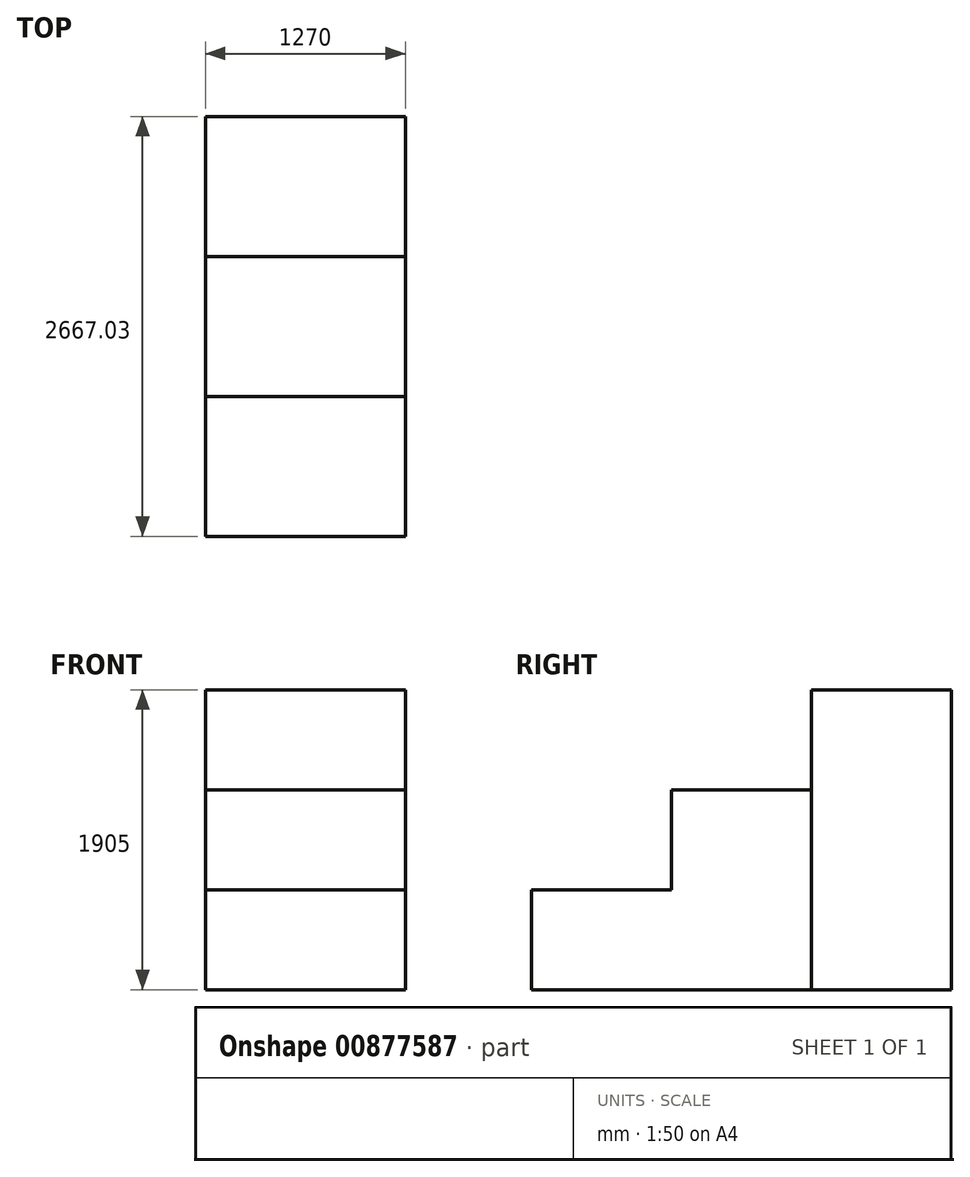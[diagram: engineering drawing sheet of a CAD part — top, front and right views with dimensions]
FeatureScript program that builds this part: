
annotation { "Feature Type Name" : "Feature", "Feature Type Description" : "" }
export const myFeature = defineFeature(function(context is Context, id is Id, definition is map)
    precondition{}
    {
        {
            var Q0;
            Q0=qCreatedBy(makeId("Top.planeOp"),FACE);
            var sketch = newSketch(context, id + "F0", { "sketchPlane" : qUnion([Q0])});
            skLineSegment(sketch, "E0.bottom", {"start": v(0, 0) * mm, "end": v(1270, 0) * mm});
            skLineSegment(sketch, "E0.top", {"start": v(0, -889) * mm, "end": v(1270, -889) * mm});
            skLineSegment(sketch, "E0.left", {"start": v(0, 0) * mm, "end": v(0, -889) * mm});
            skLineSegment(sketch, "E0.right", {"start": v(1270, 0) * mm, "end": v(1270, -889) * mm});
            skSolve(sketch);
        }
        {
            var Q0;
            Q0=makeQuery(id+"F0.imprint","IMPRINT",FACE,{"disambiguationData":[TD([[makeQuery(id+"F0.imprint","IMPRINT",EDGE,{"derivedFrom":sQuery(id+"F0.wireOp",EDGE,"E0.bottom")}),-1.0]])]});
            var sketch = newSketch(context, id + "F1", { "sketchPlane" : qUnion([Q0])});
            skLineSegment(sketch, "E1.bottom", {"start": v(0, 0) * mm, "end": v(1270, 0) * mm});
            skLineSegment(sketch, "E1.top", {"start": v(0, 889) * mm, "end": v(1270, 889) * mm});
            skLineSegment(sketch, "E1.left", {"start": v(0, 0) * mm, "end": v(0, 889) * mm});
            skLineSegment(sketch, "E1.right", {"start": v(1270, 0) * mm, "end": v(1270, 889) * mm});
            skSolve(sketch);
        }
        {
            var Q0;
            Q0=makeQuery(id+"F1.imprint","IMPRINT",FACE,{"disambiguationData":[TD([[makeQuery(id+"F1.imprint","IMPRINT",EDGE,{"derivedFrom":sQuery(id+"F1.wireOp",EDGE,"E1.bottom")}),1.0]])]});
            var sketch = newSketch(context, id + "F2", { "sketchPlane" : qUnion([Q0])});
            skLineSegment(sketch, "E2.bottom", {"start": v(0, 889.03) * mm, "end": v(1270, 889.03) * mm});
            skLineSegment(sketch, "E2.top", {"start": v(0, 1778.03) * mm, "end": v(1270, 1778.03) * mm});
            skLineSegment(sketch, "E2.left", {"start": v(0, 889.03) * mm, "end": v(0, 1778.03) * mm});
            skLineSegment(sketch, "E2.right", {"start": v(1270, 889.03) * mm, "end": v(1270, 1778.03) * mm});
            skSolve(sketch);
        }
        {
            var Q0;
            Q0=makeQuery(id+"F0.imprint","IMPRINT",FACE,{"disambiguationData":[TD([[makeQuery(id+"F0.imprint","IMPRINT",EDGE,{"derivedFrom":sQuery(id+"F0.wireOp",EDGE,"E0.bottom")}),-1.0]])]});
            extrude(context, id + "F3", {"entities" : qUnion([Q0]), "depth" : 635 * mm, "offsetDistance" : 25.4 * mm});
        }
        {
            var Q0;
            Q0=makeQuery(id+"F1.imprint","IMPRINT",FACE,{"disambiguationData":[TD([[makeQuery(id+"F1.imprint","IMPRINT",EDGE,{"derivedFrom":sQuery(id+"F1.wireOp",EDGE,"E1.bottom")}),1.0]])]});
            extrude(context, id + "F4", {"entities" : qUnion([Q0]), "operationType" : NewBodyOperationType.ADD, "depth" : 1270 * mm, "offsetDistance" : 25.4 * mm});
        }
        {
            var Q0;
            Q0=makeQuery(id+"F2.imprint","IMPRINT",FACE,{"disambiguationData":[TD([[makeQuery(id+"F2.imprint","IMPRINT",EDGE,{"derivedFrom":sQuery(id+"F2.wireOp",EDGE,"E2.bottom")}),1.0]])]});
            extrude(context, id + "F5", {"entities" : qUnion([Q0]), "depth" : 1905 * mm, "offsetDistance" : 25.4 * mm});
        }
    });
